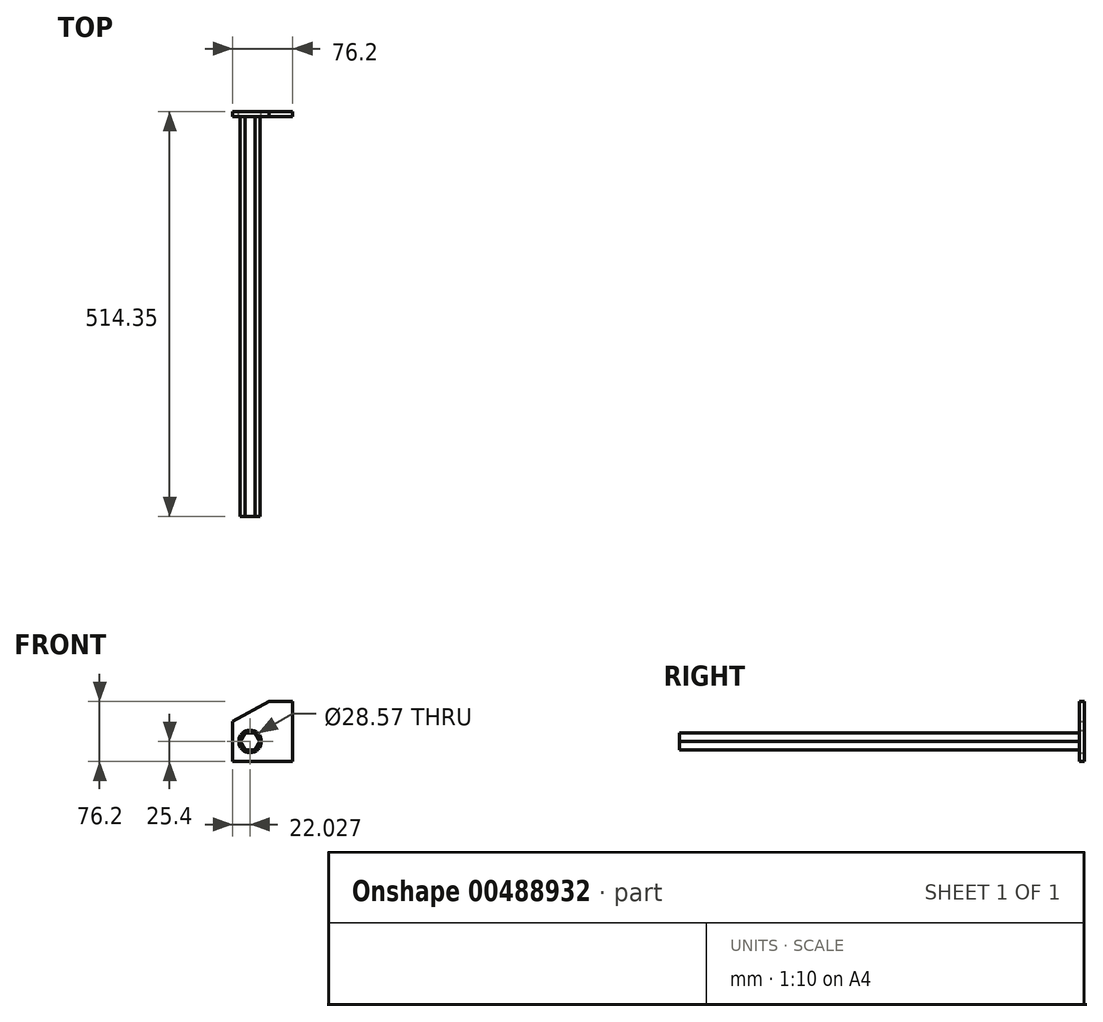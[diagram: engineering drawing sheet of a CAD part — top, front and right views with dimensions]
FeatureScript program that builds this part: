
annotation { "Feature Type Name" : "Feature", "Feature Type Description" : "" }
export const myFeature = defineFeature(function(context is Context, id is Id, definition is map)
    precondition{}
    {
        {
            var Q0;
            Q0=qCreatedBy(makeId("Front.planeOp"),FACE);
            var sketch = newSketch(context, id + "F0", { "sketchPlane" : qUnion([Q0])});
            skLineSegment(sketch, "E0", {"start": v(0, -76.2) * mm, "end": v(-76.2, -76.2) * mm});
            skLineSegment(sketch, "E1", {"start": v(-76.2, -76.2) * mm, "end": v(-76.2, -25.4) * mm});
            skLineSegment(sketch, "E2", {"start": v(-76.2, -25.4) * mm, "end": v(-30.34, 0) * mm});
            skLineSegment(sketch, "E3", {"start": v(-30.34, 0) * mm, "end": v(0, 0) * mm});
            skLineSegment(sketch, "E4", {"start": v(0, 0) * mm, "end": v(0, -76.2) * mm});
            skCircle(sketch, "E5", {"center": v(-54.17, -50.8) * mm, "radius": 14.29 * mm});
            skPoint(sketch, "E5.centerSnap0", {"position": v(-76.2, -50.8) * mm});
            skSolve(sketch);
        }
        {
            var Q0;
            Q0=makeQuery(id+"F0.imprint","IMPRINT",FACE,{"disambiguationData":[TD([[makeQuery(id+"F0.imprint","IMPRINT",EDGE,{"derivedFrom":sQuery(id+"F0.wireOp",EDGE,"E0")}),-1.0]])]});
            extrude(context, id + "F1", {"entities" : qUnion([Q0]), "depth" : 6.35 * mm, "offsetDistance" : 25.4 * mm});
        }
        {
            var Q0;
            Q0=makeQuery(id+"F1.opExtrude","CAP_FACE",FACE,{"disambiguationData":[OSD([sQuery(id+"F0.wireOp",EDGE,"E0"),sQuery(id+"F0.wireOp",EDGE,"E1"),sQuery(id+"F0.wireOp",EDGE,"E2"),sQuery(id+"F0.wireOp",EDGE,"E3"),sQuery(id+"F0.wireOp",EDGE,"E4"),sQuery(id+"F0.wireOp",EDGE,"E5")])],"isStart":false});
            var sketch = newSketch(context, id + "F2", { "sketchPlane" : qUnion([Q0])});
            skCircle(sketch, "E6.cCircle", {"center": v(-54.17, -50.8) * mm, "radius": 11 * mm, "construction": true});
            skLineSegment(sketch, "E6.0", {"start": v(-60.52, -39.8) * mm, "end": v(-47.82, -39.8) * mm});
            skLineSegment(sketch, "E6.1", {"start": v(-47.82, -39.8) * mm, "end": v(-41.47, -50.8) * mm});
            skLineSegment(sketch, "E6.2", {"start": v(-41.47, -50.8) * mm, "end": v(-47.82, -61.8) * mm});
            skLineSegment(sketch, "E6.3", {"start": v(-47.82, -61.8) * mm, "end": v(-60.52, -61.8) * mm});
            skLineSegment(sketch, "E6.4", {"start": v(-60.52, -61.8) * mm, "end": v(-66.87, -50.8) * mm});
            skLineSegment(sketch, "E6.5", {"start": v(-66.87, -50.8) * mm, "end": v(-60.52, -39.8) * mm});
            skPoint(sketch, "E6.0.midPoint", {"position": v(-54.17, -39.8) * mm});
            skSolve(sketch);
        }
        {
            var Q0;
            Q0=makeQuery(id+"F2.imprint","IMPRINT",FACE,{"disambiguationData":[TD([[makeQuery(id+"F2.imprint","IMPRINT",EDGE,{"derivedFrom":sQuery(id+"F2.wireOp",EDGE,"E6.0")}),-1.0]])]});
            extrude(context, id + "F3", {"entities" : qUnion([Q0]), "depth" : 508 * mm, "offsetDistance" : 25.4 * mm});
        }
    });
